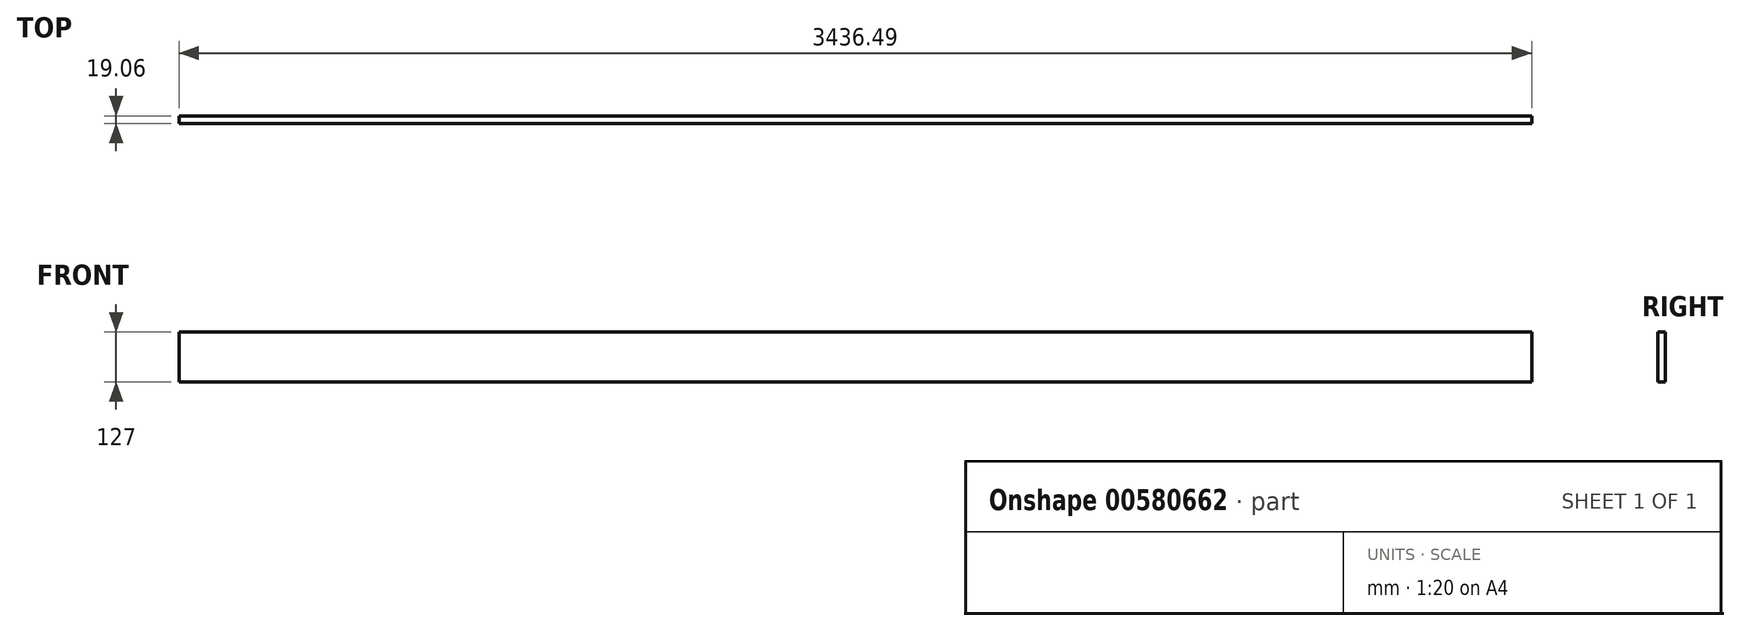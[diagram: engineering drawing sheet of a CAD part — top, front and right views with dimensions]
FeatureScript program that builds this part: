
annotation { "Feature Type Name" : "Feature", "Feature Type Description" : "" }
export const myFeature = defineFeature(function(context is Context, id is Id, definition is map)
    precondition{}
    {
        {
            var Q0;
            Q0=qCreatedBy(makeId("Top.planeOp"),FACE);
            var sketch = newSketch(context, id + "F0", { "sketchPlane" : qUnion([Q0])});
            skLineSegment(sketch, "E0.bottom", {"start": v(-236.98, -9.53) * mm, "end": v(-3673.47, -9.53) * mm});
            skLineSegment(sketch, "E0.top", {"start": v(-236.98, 9.52) * mm, "end": v(-3673.47, 9.52) * mm});
            skPoint(sketch, "E0.middle", {"position": v(0, 0) * mm});
            skPoint(sketch, "E1.orphan", {"position": v(217.93, 9.53) * mm});
            skPoint(sketch, "E0.left.end.orphan", {"position": v(3692.52, 9.53) * mm});
            skLineSegment(sketch, "E2", {"start": v(-3673.47, 9.52) * mm, "end": v(-3673.47, -9.53) * mm});
            skLineSegment(sketch, "E3", {"start": v(-236.98, 9.52) * mm, "end": v(-236.98, -9.53) * mm});
            skSolve(sketch);
        }
        {
            var Q0;
            Q0=makeQuery(id+"F0.imprint","IMPRINT",FACE,{"disambiguationData":[TD([[makeQuery(id+"F0.imprint","IMPRINT",EDGE,{"derivedFrom":sQuery(id+"F0.wireOp",EDGE,"E0.bottom")}),-1.0]])]});
            extrude(context, id + "F1", {"entities" : qUnion([Q0]), "depth" : 127 * mm, "offsetDistance" : 25.4 * mm});
        }
    });
